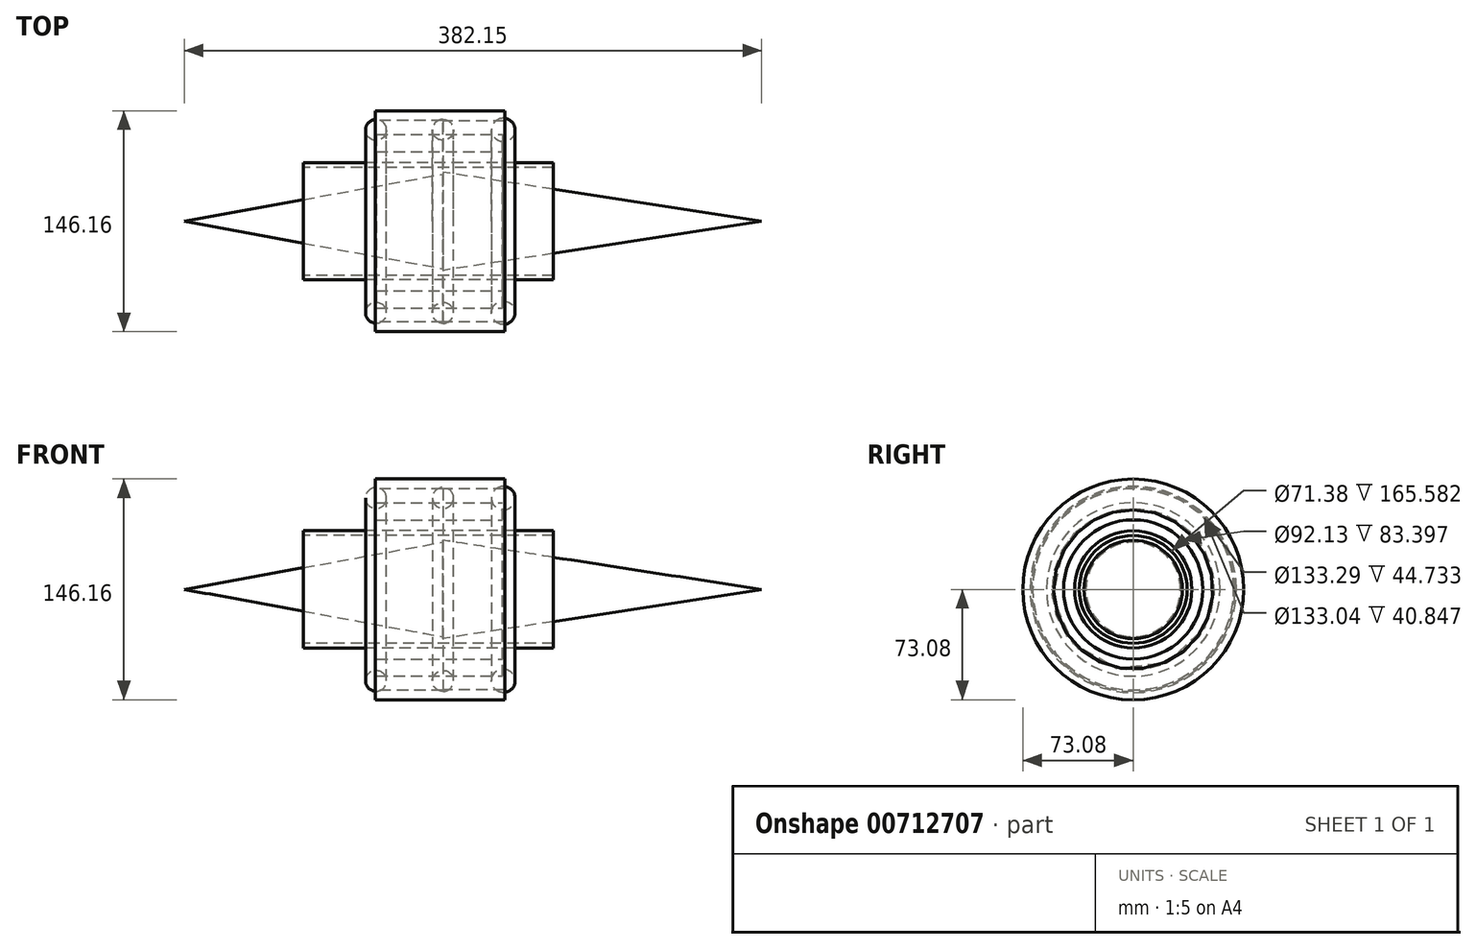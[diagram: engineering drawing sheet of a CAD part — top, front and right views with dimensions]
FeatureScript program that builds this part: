
annotation { "Feature Type Name" : "Feature", "Feature Type Description" : "" }
export const myFeature = defineFeature(function(context is Context, id is Id, definition is map)
    precondition{}
    {
        {
            var Q0;
            Q0=qCreatedBy(makeId("Right.planeOp"),FACE);
            var sketch = newSketch(context, id + "F0", { "sketchPlane" : qUnion([Q0])});
            skCircle(sketch, "E0", {"center": v(0, 0) * mm, "radius": 38.82 * mm});
            skCircle(sketch, "E1", {"center": v(0, 0) * mm, "radius": 35.7 * mm});
            skSolve(sketch);
        }
        {
            var Q0;
            Q0=makeQuery(id+"F0.imprint","IMPRINT",FACE,{"disambiguationData":[TD([[makeQuery(id+"F0.imprint","IMPRINT",EDGE,{"derivedFrom":sQuery(id+"F0.wireOp",EDGE,"E0")}),1.0]])]});
            extrude(context, id + "F1", {"entities" : qUnion([Q0]), "depth" : 73.05 * mm, "offsetDistance" : 25.4 * mm});
        }
        {
            var Q0;
            Q0=makeQuery(id+"F1.opExtrude","CAP_FACE",FACE,{"disambiguationData":[OSD([sQuery(id+"F0.wireOp",EDGE,"E0"),sQuery(id+"F0.wireOp",EDGE,"E1")])],"isStart":true});
            extrude(context, id + "F2", {"entities" : qUnion([Q0]), "operationType" : NewBodyOperationType.ADD, "depth" : 92.54 * mm, "offsetDistance" : 25.4 * mm});
        }
        {
            var Q0;
            Q0=qCreatedBy(makeId("Front.planeOp"),FACE);
            var sketch = newSketch(context, id + "F3", { "sketchPlane" : qUnion([Q0])});
            skLineSegment(sketch, "E2", {"start": v(-101.67, 0) * mm, "end": v(0, 0) * mm, "construction": true});
            skLineSegment(sketch, "E3", {"start": v(0, 0) * mm, "end": v(76.72, 0) * mm, "construction": true});
            skSolve(sketch);
        }
        {
            var Q0;
            Q0=qCreatedBy(makeId("Front.planeOp"),FACE);
            var sketch = newSketch(context, id + "F4", { "sketchPlane" : qUnion([Q0])});
            skLineSegment(sketch, "E4", {"start": v(0, 0) * mm, "end": v(0, 32.54) * mm});
            skLineSegment(sketch, "E5", {"start": v(0, 32.54) * mm, "end": v(210.93, 0) * mm});
            skLineSegment(sketch, "E6", {"start": v(210.93, 0) * mm, "end": v(0, 0) * mm});
            skSolve(sketch);
        }
        {
            var Q0;
            Q0=makeQuery(id+"F4.imprint","IMPRINT",FACE,{"disambiguationData":[TD([[makeQuery(id+"F4.imprint","IMPRINT",EDGE,{"derivedFrom":sQuery(id+"F4.wireOp",EDGE,"E4")}),-1.0]])]});
            var Q1;
            Q1=sQuery(id+"F4.wireOp",EDGE,"E6");
            revolve(context, id + "F5", {"surfaceOperationType" : NewSurfaceOperationType.NEW, "entities" : qUnion([Q0]), "axis" : qUnion([Q1]), "revolveType" : RevolveType.FULL});
        }
        {
            var Q0;
            Q0=qCreatedBy(makeId("Front.planeOp"),FACE);
            var sketch = newSketch(context, id + "F6", { "sketchPlane" : qUnion([Q0])});
            skCircle(sketch, "E7", {"center": v(0, 60.55) * mm, "radius": 6.96 * mm});
            skCircle(sketch, "E8", {"center": v(-44.3, 60.47) * mm, "radius": 6.95 * mm});
            skCircle(sketch, "E9", {"center": v(39.92, 60.47) * mm, "radius": 7.79 * mm});
            skSolve(sketch);
        }
        {
            var Q0;
            Q0=makeQuery(id+"F6.imprint","IMPRINT",FACE,{"disambiguationData":[TD([[makeQuery(id+"F6.imprint","IMPRINT",EDGE,{"derivedFrom":sQuery(id+"F6.wireOp",EDGE,"E8")}),1.0]])]});
            var Q1;
            Q1=makeQuery(id+"F6.imprint","IMPRINT",FACE,{"disambiguationData":[TD([[makeQuery(id+"F6.imprint","IMPRINT",EDGE,{"derivedFrom":sQuery(id+"F6.wireOp",EDGE,"E7")}),1.0]])]});
            var Q2;
            Q2=makeQuery(id+"F6.imprint","IMPRINT",FACE,{"disambiguationData":[TD([[makeQuery(id+"F6.imprint","IMPRINT",EDGE,{"derivedFrom":sQuery(id+"F6.wireOp",EDGE,"E9")}),1.0]])]});
            var Q3;
            Q3=sQuery(id+"F3.wireOp",EDGE,"E3");
            revolve(context, id + "F7", {"surfaceOperationType" : NewSurfaceOperationType.NEW, "entities" : qUnion([Q0, Q1, Q2]), "axis" : qUnion([Q3]), "revolveType" : RevolveType.FULL});
        }
        {
            var Q0;
            Q0=qCreatedBy(makeId("Front.planeOp"),FACE);
            var sketch = newSketch(context, id + "F8", { "sketchPlane" : qUnion([Q0])});
            skLineSegment(sketch, "E10", {"start": v(0, 0) * mm, "end": v(0, 31.3) * mm});
            skLineSegment(sketch, "E11", {"start": v(0, 31.3) * mm, "end": v(-171.22, 0) * mm});
            skLineSegment(sketch, "E12", {"start": v(-171.22, 0) * mm, "end": v(0, 0) * mm});
            skSolve(sketch);
        }
        {
            var Q0;
            Q0=makeQuery(id+"F8.imprint","IMPRINT",FACE,{"disambiguationData":[TD([[makeQuery(id+"F8.imprint","IMPRINT",EDGE,{"derivedFrom":sQuery(id+"F8.wireOp",EDGE,"E10")}),1.0]])]});
            var Q1;
            Q1=sQuery(id+"F8.wireOp",EDGE,"E12");
            revolve(context, id + "F9", {"operationType" : NewBodyOperationType.ADD, "surfaceOperationType" : NewSurfaceOperationType.NEW, "entities" : qUnion([Q0]), "axis" : qUnion([Q1]), "revolveType" : RevolveType.FULL});
        }
        {
            var Q0;
            Q0=qCreatedBy(makeId("Front.planeOp"),FACE);
            var sketch = newSketch(context, id + "F10", { "sketchPlane" : qUnion([Q0])});
            skLineSegment(sketch, "E13.bottom", {"start": v(0, 57.42) * mm, "end": v(39.24, 57.42) * mm});
            skLineSegment(sketch, "E13.top", {"start": v(0, 46.07) * mm, "end": v(39.24, 46.07) * mm});
            skLineSegment(sketch, "E13.left", {"start": v(0, 57.42) * mm, "end": v(0, 46.07) * mm});
            skLineSegment(sketch, "E13.right", {"start": v(39.24, 57.42) * mm, "end": v(39.24, 46.07) * mm});
            skLineSegment(sketch, "E14.bottom", {"start": v(0, 57.42) * mm, "end": v(-44.16, 57.42) * mm});
            skLineSegment(sketch, "E14.top", {"start": v(0, 46.07) * mm, "end": v(-44.16, 46.07) * mm});
            skLineSegment(sketch, "E14.right", {"start": v(-44.16, 57.42) * mm, "end": v(-44.16, 46.07) * mm});
            skSolve(sketch);
        }
        {
            var Q0;
            Q0=makeQuery(id+"F10.imprint","IMPRINT",FACE,{"disambiguationData":[TD([[makeQuery(id+"F10.imprint","IMPRINT",EDGE,{"derivedFrom":sQuery(id+"F10.wireOp",EDGE,"E13.bottom")}),-1.0]])]});
            var Q1;
            Q1=makeQuery(id+"F10.imprint","IMPRINT",FACE,{"disambiguationData":[TD([[makeQuery(id+"F10.imprint","IMPRINT",EDGE,{"derivedFrom":sQuery(id+"F10.wireOp",EDGE,"E14.bottom")}),1.0]])]});
            var Q2;
            {var subQ0=sQuery(id+"F0.wireOp",EDGE,"E0");Q2=makeQuery(id+"F2.boolean.opBoolean","MERGE",FACE,{"derivedFrom":[makeQuery(id+"F1.opExtrude","SWEPT_FACE",FACE,{"disambiguationData":[OSD([subQ0])]}),makeQuery(id+"F2.opExtrude","SWEPT_FACE",FACE,{"disambiguationData":[OSD([subQ0])]})]});}
            revolve(context, id + "F11", {"surfaceOperationType" : NewSurfaceOperationType.NEW, "entities" : qUnion([Q0, Q1]), "axis" : qUnion([Q2]), "revolveType" : RevolveType.FULL});
        }
        {
            var Q0;
            Q0=qCreatedBy(makeId("Front.planeOp"),FACE);
            var sketch = newSketch(context, id + "F12", { "sketchPlane" : qUnion([Q0])});
            skLineSegment(sketch, "E15.bottom", {"start": v(0, 73.08) * mm, "end": v(40.85, 73.08) * mm});
            skLineSegment(sketch, "E15.top", {"start": v(0, 66.52) * mm, "end": v(40.85, 66.52) * mm});
            skLineSegment(sketch, "E15.left", {"start": v(0, 73.08) * mm, "end": v(0, 66.52) * mm});
            skLineSegment(sketch, "E15.right", {"start": v(40.85, 73.08) * mm, "end": v(40.85, 66.52) * mm});
            skLineSegment(sketch, "E16.bottom", {"start": v(0, 73.08) * mm, "end": v(-44.73, 73.08) * mm});
            skLineSegment(sketch, "E16.top", {"start": v(0, 66.65) * mm, "end": v(-44.73, 66.65) * mm});
            skLineSegment(sketch, "E16.left", {"start": v(0, 73.08) * mm, "end": v(0, 66.65) * mm});
            skLineSegment(sketch, "E16.right", {"start": v(-44.73, 73.08) * mm, "end": v(-44.73, 66.65) * mm});
            skSolve(sketch);
        }
        {
            var Q0;
            Q0=makeQuery(id+"F12.imprint","IMPRINT",FACE,{"disambiguationData":[TD([[makeQuery(id+"F12.imprint","IMPRINT",EDGE,{"derivedFrom":sQuery(id+"F12.wireOp",EDGE,"E15.bottom")}),-1.0]])]});
            var Q1;
            Q1=makeQuery(id+"F12.imprint","IMPRINT",FACE,{"disambiguationData":[TD([[makeQuery(id+"F12.imprint","IMPRINT",EDGE,{"derivedFrom":sQuery(id+"F12.wireOp",EDGE,"E16.bottom")}),1.0]])]});
            var Q2;
            Q2=makeQuery(id+"F11.opRevolve","SWEPT_FACE",FACE,{"disambiguationData":[OSD([sQuery(id+"F10.wireOp",EDGE,"E13.bottom"),sQuery(id+"F10.wireOp",EDGE,"E14.bottom")])]});
            revolve(context, id + "F13", {"surfaceOperationType" : NewSurfaceOperationType.NEW, "entities" : qUnion([Q0, Q1]), "axis" : qUnion([Q2]), "revolveType" : RevolveType.FULL});
        }
    });
